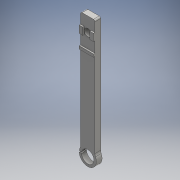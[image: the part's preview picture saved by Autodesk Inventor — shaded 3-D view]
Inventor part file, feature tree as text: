
AUTODESK INVENTOR PART (.ipt)
format: ipt  version: 2016 (Build 200138000, 138)  size: 188,928 bytes
history: native  units: mm
features: sketch x5, extrude x4, fillet x3, hole x1, draft x1, projected_geometry x1
ambient origin geometry x8: Origin, YZ Plane, XZ Plane, XY Plane, X Axis, Y Axis, Z Axis, Center Point
bodies: Solid1 (feature_tree)
feature tree (15):
  extrude  "Extrusion1"  Depth=10.0mm
  hole  "Hole1"  [1 undecoded]
  fillet  "Fillet1"  Radius=1.745329mm
  draft  "FaceDraft1"
  extrude  "Extrusion2"  Depth=4.0mm TaperAngle=0.0deg
  fillet  "Fillet2"  Radius=0.5mm
  fillet  "Fillet3"  Radius=10.0mm
  extrude  "Extrusion3"  Depth=20.0mm
  extrude  "Extrusion4"  Depth=5.0mm
  sketch  "Sketch1"  dims[d3=4.0mm d4=0.0mm d5=10.0mm]
  sketch  "Sketch2"  dims[d6=5.0mm d7=6.0mm d8=4.0mm d9=2.0mm d10=90.0deg d11=8.0mm d12=20.594885mm d13=4.0mm d14=1.745329mm]
  sketch  "Sketch3"  dims[d15=0.6mm d16=4.0mm d17=0.0mm d18=0.5mm d19=10.0mm]
  sketch  "Sketch4"  dims[d20=1.0mm d21=20.0mm]
  sketch  "Sketch5"  dims[d22=2.0mm d23=5.0mm d24=1.0mm d25=0.0mm d26=5.0mm d27=5.0mm d28=1.0mm d29=0.0mm]
  projected_geometry  "Projected Loop1"
note: 1 required parameter value undecoded (feature->parameter linkage not recoverable at this tier; creation-order binding heuristic only, values carry confidence <= 0.55)
